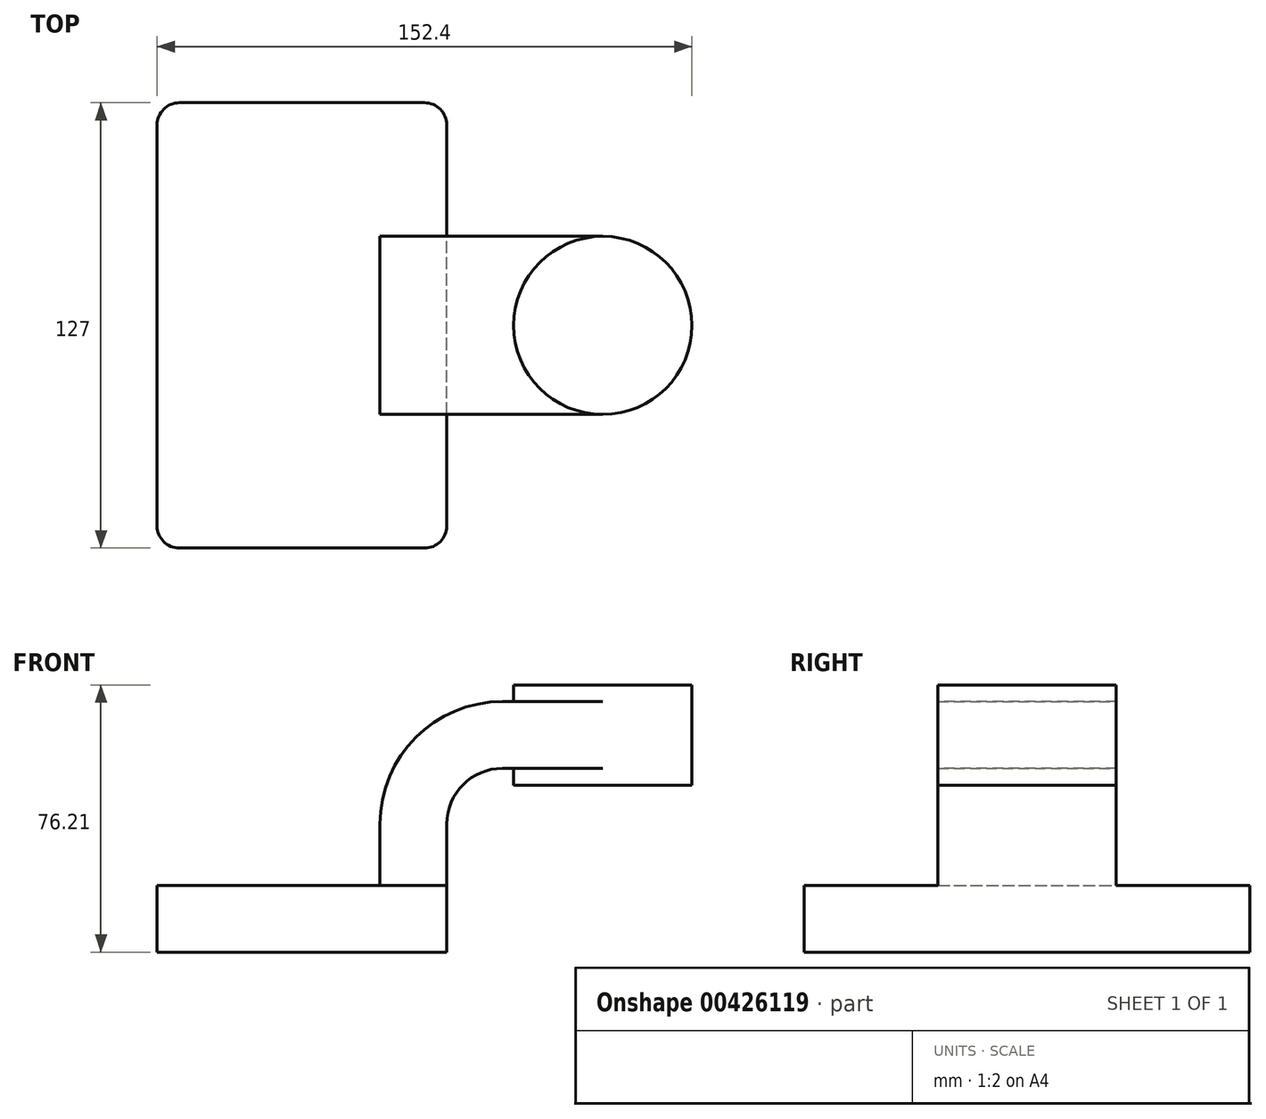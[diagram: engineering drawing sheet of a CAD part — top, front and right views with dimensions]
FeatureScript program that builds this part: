
annotation { "Feature Type Name" : "Feature", "Feature Type Description" : "" }
export const myFeature = defineFeature(function(context is Context, id is Id, definition is map)
    precondition{}
    {
        {
            var Q0;
            Q0=qCreatedBy(makeId("Front.planeOp"),FACE);
            var sketch = newSketch(context, id + "F0", { "sketchPlane" : qUnion([Q0])});
            skLineSegment(sketch, "E0.bottom", {"start": v(-41.28, 9.52) * mm, "end": v(41.27, 9.53) * mm});
            skLineSegment(sketch, "E0.top", {"start": v(-41.28, -9.53) * mm, "end": v(41.28, -9.53) * mm});
            skLineSegment(sketch, "E0.left", {"start": v(-41.28, 9.52) * mm, "end": v(-41.28, -9.53) * mm});
            skLineSegment(sketch, "E0.right", {"start": v(41.27, 9.53) * mm, "end": v(41.28, -9.52) * mm});
            skPoint(sketch, "E0.middle", {"position": v(0, 0) * mm});
            skLineSegment(sketch, "E1.bottom", {"start": v(60.33, 38.1) * mm, "end": v(111.13, 38.1) * mm});
            skLineSegment(sketch, "E1.top", {"start": v(60.33, 66.68) * mm, "end": v(111.13, 66.68) * mm});
            skLineSegment(sketch, "E1.left", {"start": v(60.33, 38.1) * mm, "end": v(60.33, 66.67) * mm});
            skLineSegment(sketch, "E1.right", {"start": v(111.13, 38.1) * mm, "end": v(111.13, 66.68) * mm});
            skPoint(sketch, "E1.middle", {"position": v(85.72, 52.39) * mm});
            skLineSegment(sketch, "E2", {"start": v(41.27, 9.53) * mm, "end": v(41.27, 27) * mm});
            skArc(sketch, "E3", {"start": v(41.27, 27) * mm, "mid": v(45.92, 38.23) * mm, "end": v(57.15, 42.88) * mm});
            skLineSegment(sketch, "E4", {"start": v(57.15, 42.88) * mm, "end": v(85.73, 42.88) * mm});
            skLineSegment(sketch, "E5.0", {"start": v(57.15, 61.93) * mm, "end": v(85.73, 61.93) * mm});
            skArc(sketch, "E5.1", {"start": v(22.22, 27) * mm, "mid": v(32.45, 51.7) * mm, "end": v(57.15, 61.93) * mm});
            skLineSegment(sketch, "E5.2", {"start": v(22.22, 9.53) * mm, "end": v(22.22, 27) * mm});
            skFitSpline(sketch, "E6", {"points": [v(-41.28, 9.52) * mm, v(57.15, 61.93) * mm], "startDerivative": vector(79.45, 115.56) * mm, "endDerivative": vector(104.4, -0.76) * mm});
            skLineSegment(sketch, "E7", {"start": v(85.73, 66.68) * mm, "end": v(85.73, 38.1) * mm});
            skSolve(sketch);
        }
        {
            var Q0;
            Q0=makeQuery(id+"F0.imprint","IMPRINT",FACE,{"disambiguationData":[TD([[makeQuery(id+"F0.imprint","IMPRINT",EDGE,{"derivedFrom":sQuery(id+"F0.wireOp",EDGE,"E0.top")}),1.0]])]});
            extrude(context, id + "F1", {"entities" : qUnion([Q0]), "endBound" : BoundingType.SYMMETRIC, "depth" : 127 * mm});
        }
        {
            var Q0;
            {var subQ0=sQuery(id+"F0.wireOp",EDGE,"E4");var subQ1=sQuery(id+"F0.wireOp",EDGE,"E1.left");var subQ2=makeQuery(id+"F0.imprint","INTERSECT",VERTEX,{"derivedFrom":[subQ1,subQ0]});Q0=makeQuery(id+"F0.imprint","IMPRINT",FACE,{"disambiguationData":[TD([[makeQuery(id+"F0.imprint","IMPRINT",EDGE,{"disambiguationData":[TD([[subQ2,-1.0]])],"derivedFrom":subQ1}),-1.0]])]});}
            var Q1;
            {var subQ1=sQuery(id+"F0.wireOp",EDGE,"E2");Q1=makeQuery(id+"F0.imprint","IMPRINT",FACE,{"disambiguationData":[TD([[makeQuery(id+"F0.imprint","IMPRINT",EDGE,{"derivedFrom":subQ1}),1.0]])]});}
            extrude(context, id + "F2", {"entities" : qUnion([Q0, Q1]), "operationType" : NewBodyOperationType.ADD, "endBound" : BoundingType.SYMMETRIC, "depth" : 50.8 * mm});
        }
        {
            var Q0;
            Q0=makeQuery(id+"F0.imprint","IMPRINT",FACE,{"disambiguationData":[TD([[makeQuery(id+"F0.imprint","IMPRINT",EDGE,{"derivedFrom":sQuery(id+"F0.wireOp",EDGE,"E5.1")}),1.0]])]});
            extrude(context, id + "F3", {"entities" : qUnion([Q0]), "operationType" : NewBodyOperationType.ADD, "endBound" : BoundingType.SYMMETRIC, "depth" : 15.88 * mm});
        }
        {
            var Q0;
            {var subQ4=sQuery(id+"F0.wireOp",EDGE,"E1.right");Q0=makeQuery(id+"F0.imprint","IMPRINT",FACE,{"disambiguationData":[TD([[makeQuery(id+"F0.imprint","IMPRINT",EDGE,{"derivedFrom":subQ4}),1.0]])]});}
            var Q1;
            Q1=sQuery(id+"F0.wireOp",EDGE,"E7");
            revolve(context, id + "F4", {"operationType" : NewBodyOperationType.ADD, "entities" : qUnion([Q0]), "axis" : qUnion([Q1]), "revolveType" : RevolveType.FULL});
        }
        {
            var Q0;
            Q0=makeQuery(id+"F1.opExtrude","CAP_EDGE",EDGE,{"disambiguationData":[OSD([sQuery(id+"F0.wireOp",EDGE,"E0.left")])],"isStart":false});
            var Q1;
            Q1=makeQuery(id+"F1.opExtrude","CAP_EDGE",EDGE,{"disambiguationData":[OSD([sQuery(id+"F0.wireOp",EDGE,"E0.right")])],"isStart":false});
            var Q2;
            Q2=makeQuery(id+"F1.opExtrude","CAP_EDGE",EDGE,{"disambiguationData":[OSD([sQuery(id+"F0.wireOp",EDGE,"E0.right")])],"isStart":true});
            var Q3;
            Q3=makeQuery(id+"F1.opExtrude","CAP_EDGE",EDGE,{"disambiguationData":[OSD([sQuery(id+"F0.wireOp",EDGE,"E0.left")])],"isStart":true});
            fillet(context, id + "F5", {"entities" : qUnion([Q0, Q1, Q2, Q3]), "radius" : 6.35 * mm, "tangentPropagation" : true, "allowEdgeOverflow" : false});
        }
    });
